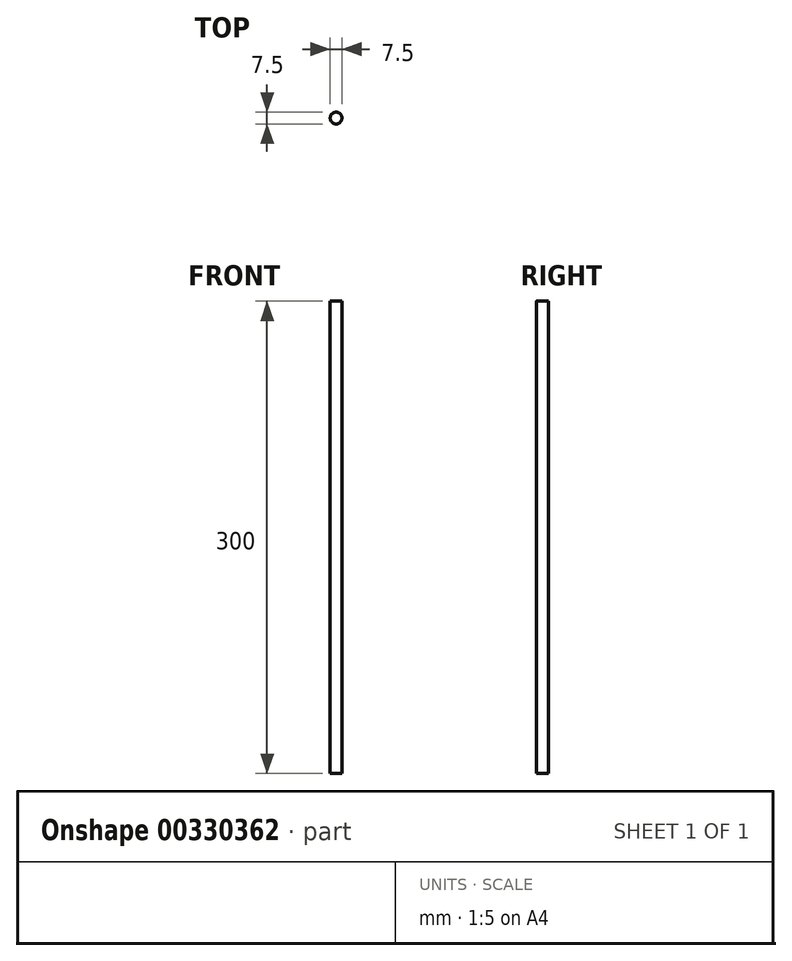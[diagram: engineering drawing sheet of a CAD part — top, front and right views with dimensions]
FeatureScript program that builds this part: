
annotation { "Feature Type Name" : "Feature", "Feature Type Description" : "" }
export const myFeature = defineFeature(function(context is Context, id is Id, definition is map)
    precondition{}
    {
        {
            var Q0;
            Q0=qCreatedBy(makeId("Top.planeOp"),FACE);
            var sketch = newSketch(context, id + "F0", { "sketchPlane" : qUnion([Q0])});
            skCircle(sketch, "E0", {"center": v(0, 0) * mm, "radius": 3.75 * mm});
            skSolve(sketch);
        }
        {
            var Q0;
            Q0=makeQuery(id+"F0.imprint","IMPRINT",FACE,{"disambiguationData":[TD([[makeQuery(id+"F0.imprint","IMPRINT",EDGE,{"derivedFrom":sQuery(id+"F0.wireOp",EDGE,"E0")}),1.0]])]});
            extrude(context, id + "F1", {"entities" : qUnion([Q0]), "depth" : 300 * mm, "offsetDistance" : 25 * mm});
        }
    });
